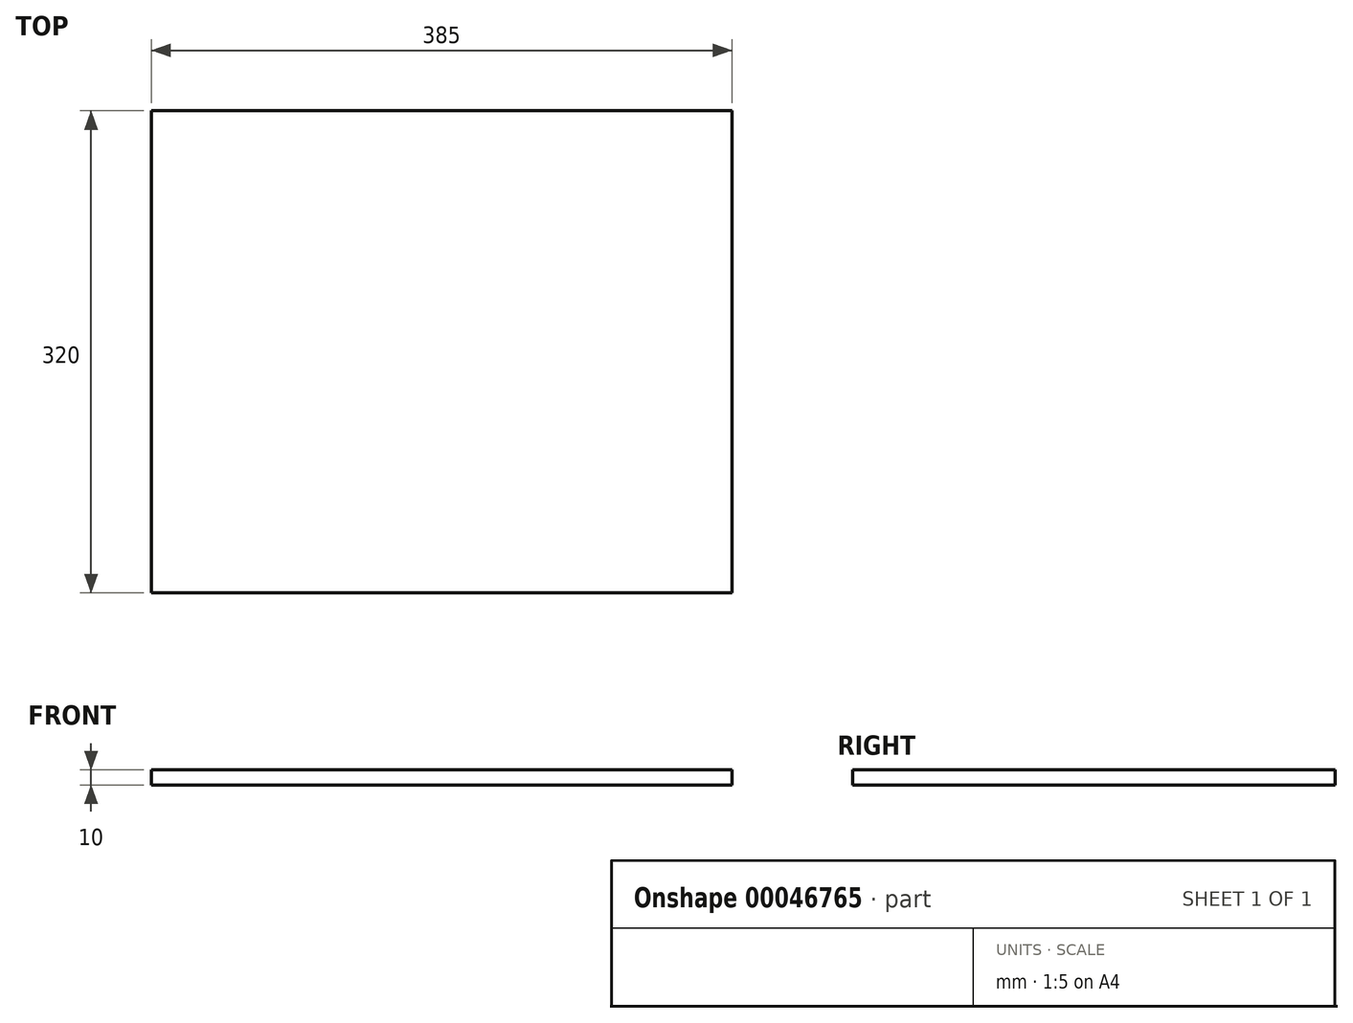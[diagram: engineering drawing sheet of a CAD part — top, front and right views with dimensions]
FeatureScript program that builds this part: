
annotation { "Feature Type Name" : "Feature", "Feature Type Description" : "" }
export const myFeature = defineFeature(function(context is Context, id is Id, definition is map)
    precondition{}
    {
        {
            var Q0;
            Q0=qCreatedBy(makeId("Top.planeOp"),FACE);
            var sketch = newSketch(context, id + "F0", { "sketchPlane" : qUnion([Q0])});
            skLineSegment(sketch, "E0.bottom", {"start": v(-70.96, 65.05) * mm, "end": v(314.04, 65.05) * mm});
            skLineSegment(sketch, "E0.top", {"start": v(-70.96, -254.95) * mm, "end": v(314.04, -254.95) * mm});
            skLineSegment(sketch, "E0.left", {"start": v(-70.96, 65.05) * mm, "end": v(-70.96, -254.95) * mm});
            skLineSegment(sketch, "E0.right", {"start": v(314.04, 65.05) * mm, "end": v(314.04, -254.95) * mm});
            skSolve(sketch);
        }
        {
            var Q0;
            Q0=qSketchRegion(id+"F0",true);
            extrude(context, id + "F1", {"entities" : qUnion([Q0]), "depth" : 10 * mm});
        }
    });
